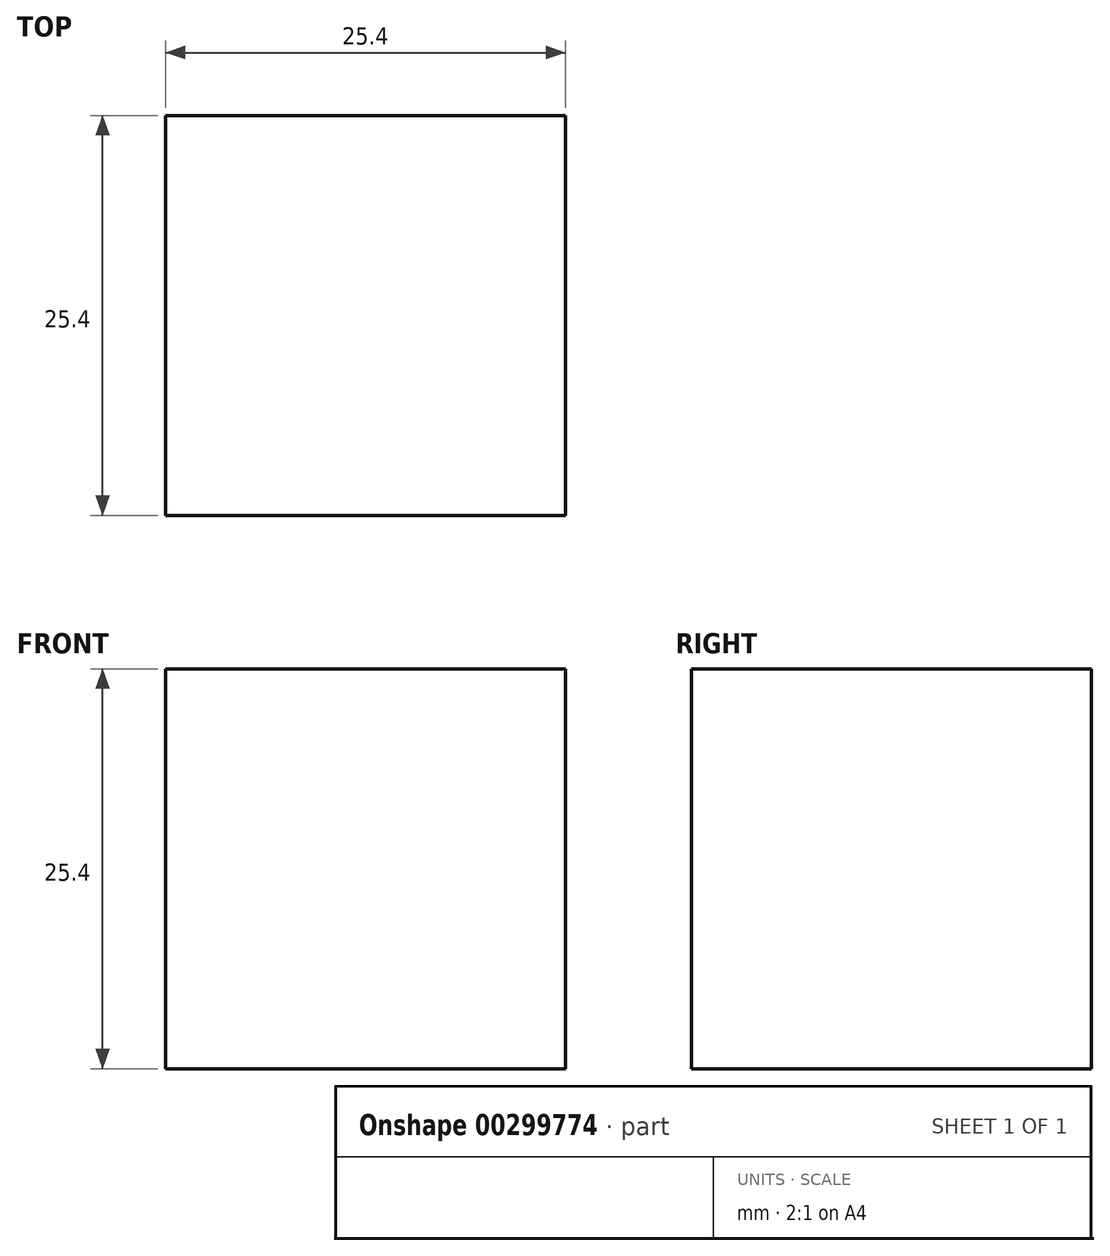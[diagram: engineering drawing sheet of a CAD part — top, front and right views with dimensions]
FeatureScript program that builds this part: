
annotation { "Feature Type Name" : "Feature", "Feature Type Description" : "" }
export const myFeature = defineFeature(function(context is Context, id is Id, definition is map)
    precondition{}
    {
        {
            var Q0;
            Q0=qCreatedBy(makeId("Front.planeOp"),FACE);
            var sketch = newSketch(context, id + "F0", { "sketchPlane" : qUnion([Q0])});
            skLineSegment(sketch, "E0", {"start": v(0, 25.4) * mm, "end": v(0, 0) * mm});
            skLineSegment(sketch, "E1", {"start": v(0, 0) * mm, "end": v(-25.4, 0) * mm});
            skLineSegment(sketch, "E2", {"start": v(-25.4, 0) * mm, "end": v(-25.4, 25.4) * mm});
            skLineSegment(sketch, "E3", {"start": v(-25.4, 25.4) * mm, "end": v(0, 25.4) * mm});
            skSolve(sketch);
        }
        {
            var Q0;
            Q0 = qSketchRegion(id + "F0", true);
            extrude(context, id + "F1", {"entities" : qUnion([Q0]), "depth" : 25.4 * mm});
        }
    });
